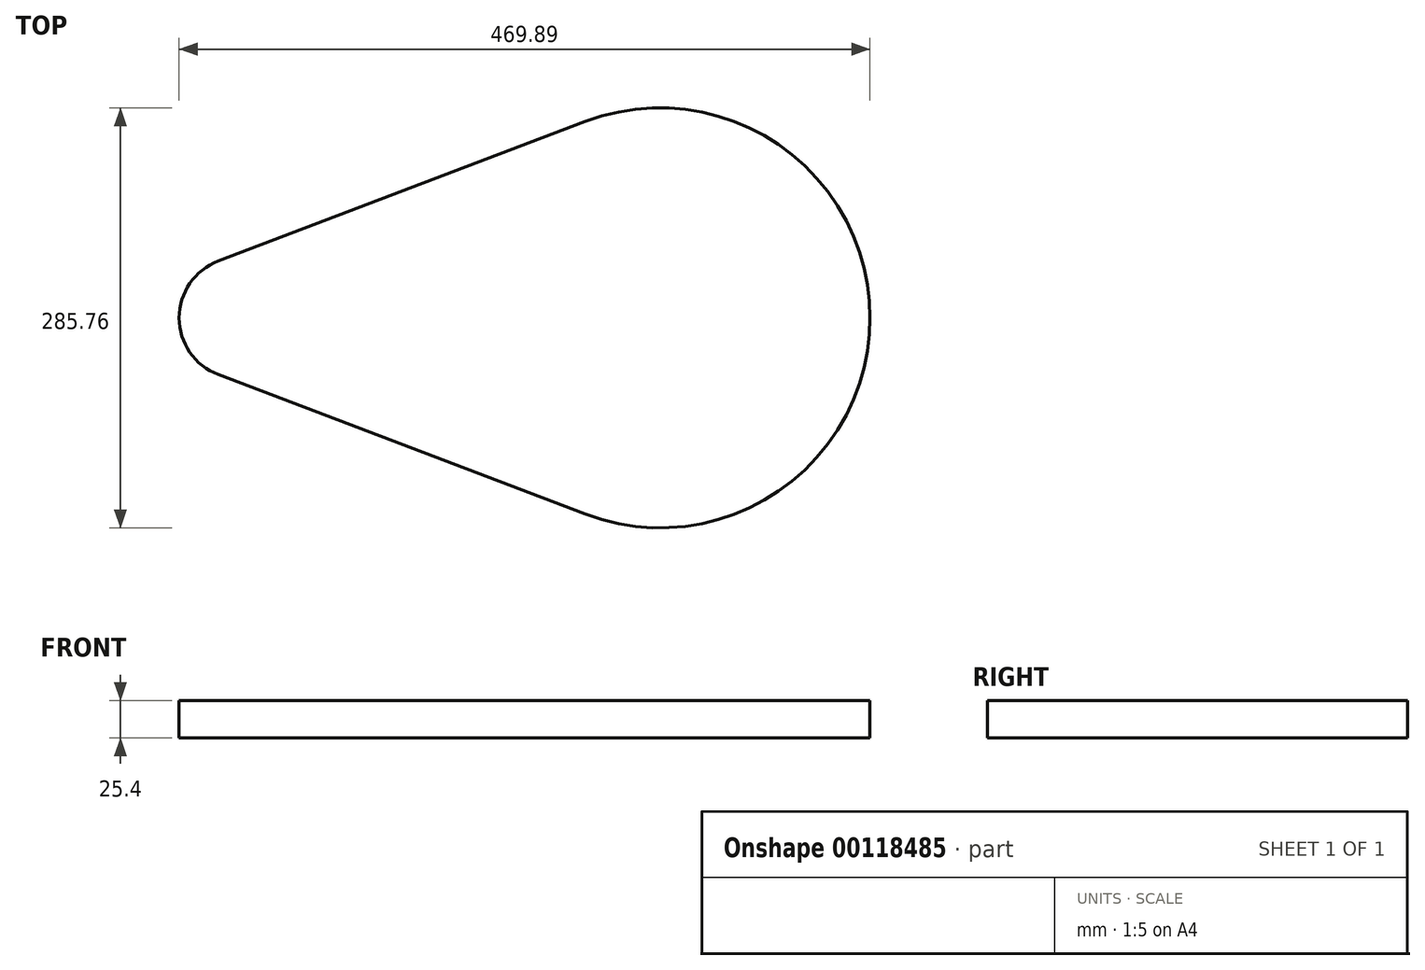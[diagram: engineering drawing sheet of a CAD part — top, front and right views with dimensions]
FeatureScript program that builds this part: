
annotation { "Feature Type Name" : "Feature", "Feature Type Description" : "" }
export const myFeature = defineFeature(function(context is Context, id is Id, definition is map)
    precondition{}
    {
        {
            var Q0;
            Q0=qCreatedBy(makeId("Top.planeOp"),FACE);
            var sketch = newSketch(context, id + "F0", { "sketchPlane" : qUnion([Q0])});
            skArc(sketch, "E0", {"start": v(-14.68, 38.58) * mm, "mid": v(-41.28, 0) * mm, "end": v(-14.68, -38.58) * mm});
            skArc(sketch, "E1", {"start": v(234.95, -133.54) * mm, "mid": v(428.63, 0) * mm, "end": v(234.95, 133.54) * mm});
            skLineSegment(sketch, "E2", {"start": v(-14.68, -38.58) * mm, "end": v(234.95, -133.54) * mm});
            skLineSegment(sketch, "E3", {"start": v(-14.68, 38.58) * mm, "end": v(234.95, 133.54) * mm});
            skSolve(sketch);
        }
        {
            var Q0;
            Q0=makeQuery(id+"F0.imprint","IMPRINT",FACE,{"disambiguationData":[TD([[makeQuery(id+"F0.imprint","IMPRINT",EDGE,{"derivedFrom":sQuery(id+"F0.wireOp",EDGE,"E0")}),1.0]])]});
            extrude(context, id + "F1", {"entities" : qUnion([Q0]), "depth" : 25.4 * mm});
        }
    });
